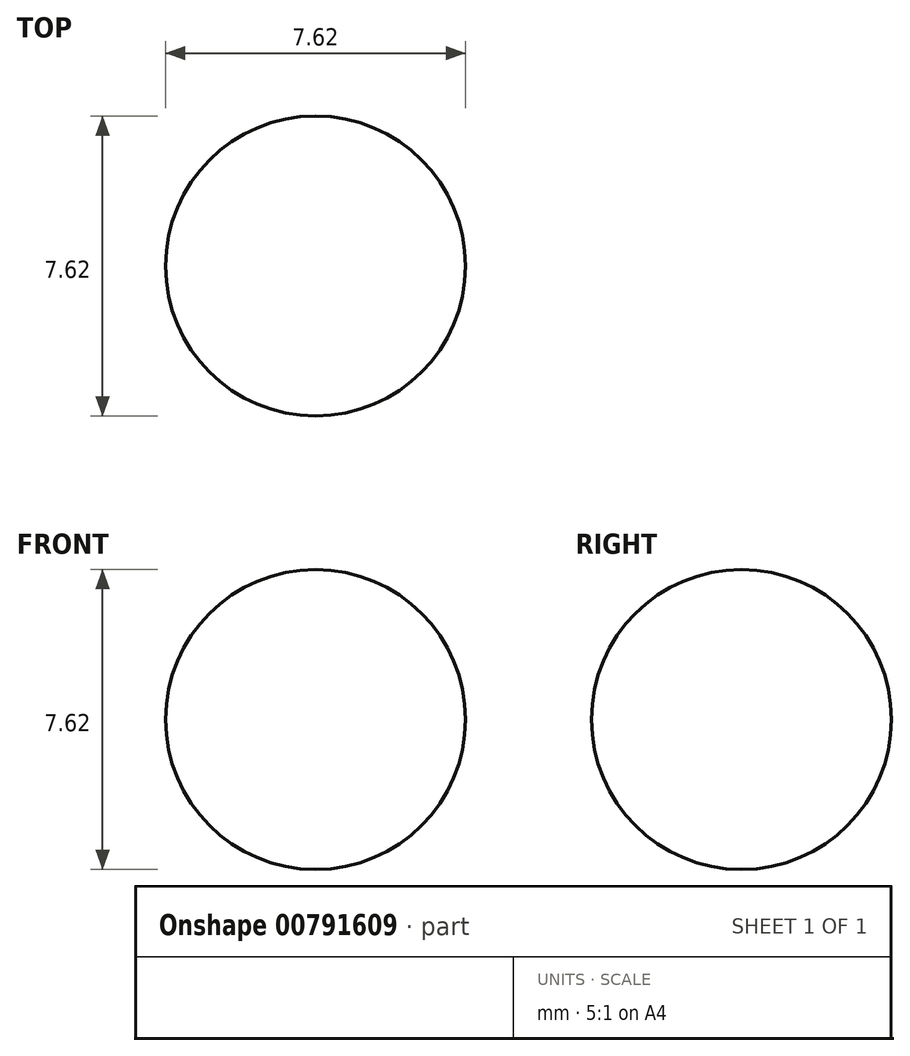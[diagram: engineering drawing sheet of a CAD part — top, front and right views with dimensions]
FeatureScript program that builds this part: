
annotation { "Feature Type Name" : "Feature", "Feature Type Description" : "" }
export const myFeature = defineFeature(function(context is Context, id is Id, definition is map)
    precondition{}
    {
        {
            var Q0;
            Q0=qCreatedBy(makeId("Front.planeOp"),FACE);
            var sketch = newSketch(context, id + "F0", { "sketchPlane" : qUnion([Q0])});
            skArc(sketch, "E0", {"start": v(0, 3.81) * mm, "mid": v(-3.81, 0) * mm, "end": v(0, -3.81) * mm});
            skLineSegment(sketch, "E1", {"start": v(0, 3.81) * mm, "end": v(0, -3.81) * mm});
            skSolve(sketch);
        }
        {
            var Q0;
            Q0 = qSketchRegion(id + "F0", true);
            var Q1;
            Q1=sQuery(id+"F0.wireOp",EDGE,"E1");
            revolve(context, id + "F1", {"surfaceOperationType" : NewSurfaceOperationType.NEW, "entities" : qUnion([Q0]), "axis" : qUnion([Q1]), "revolveType" : RevolveType.FULL});
        }
    });
